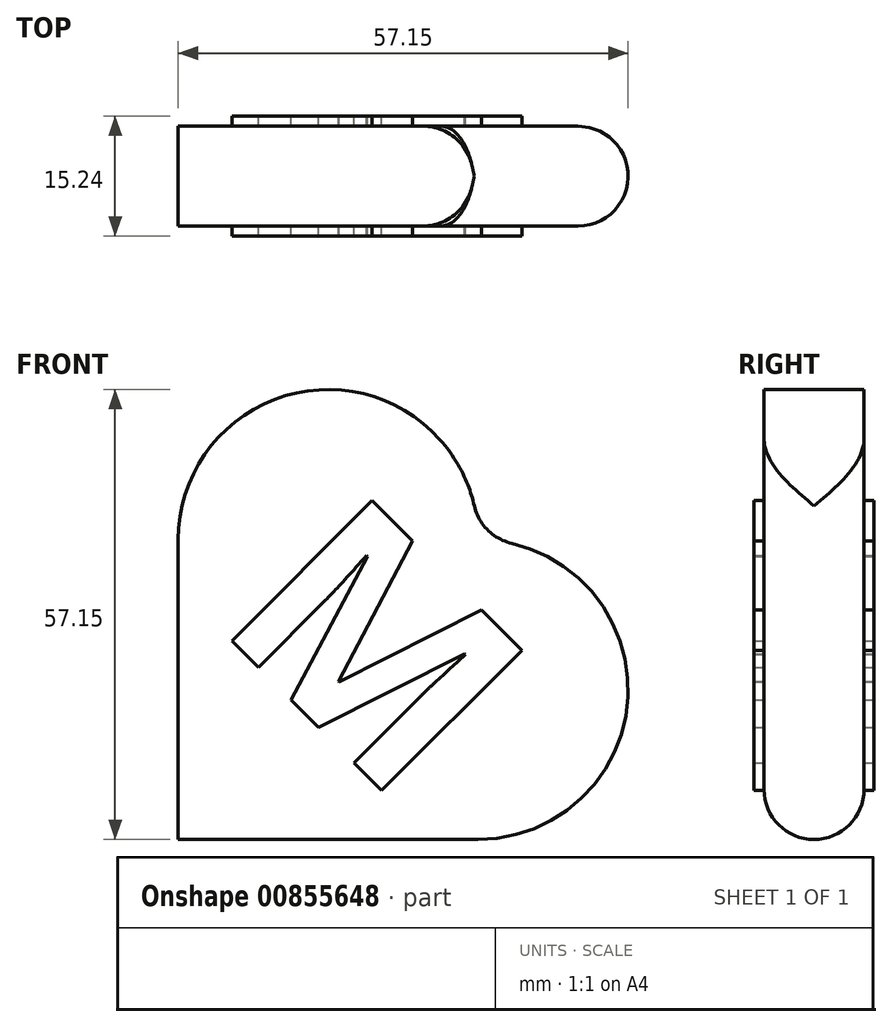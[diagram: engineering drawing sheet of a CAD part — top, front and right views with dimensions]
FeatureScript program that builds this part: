
annotation { "Feature Type Name" : "Feature", "Feature Type Description" : "" }
export const myFeature = defineFeature(function(context is Context, id is Id, definition is map)
    precondition{}
    {
        {
            var Q0;
            Q0=qCreatedBy(makeId("Front.planeOp"),FACE);
            var sketch = newSketch(context, id + "F0", { "sketchPlane" : qUnion([Q0])});
            skLineSegment(sketch, "E0.bottom", {"start": v(19.05, -19.05) * mm, "end": v(-19.05, -19.05) * mm});
            skLineSegment(sketch, "E0.top", {"start": v(19.05, 19.05) * mm, "end": v(-19.05, 19.05) * mm});
            skLineSegment(sketch, "E0.left", {"start": v(19.05, -19.05) * mm, "end": v(19.05, 19.05) * mm});
            skLineSegment(sketch, "E0.right", {"start": v(-19.05, -19.05) * mm, "end": v(-19.05, 19.05) * mm});
            skPoint(sketch, "E0.middle", {"position": v(0, 0) * mm});
            skCircle(sketch, "E1", {"center": v(0, 19.05) * mm, "radius": 19.05 * mm});
            skCircle(sketch, "E2", {"center": v(19.05, 0) * mm, "radius": 19.05 * mm});
            skSolve(sketch);
        }
        {
            var Q0;
            Q0 = qSketchRegion(id + "F0", true);
            extrude(context, id + "F1", {"entities" : qUnion([Q0]), "endBound" : BoundingType.SYMMETRIC, "depth" : 12.7 * mm, "offsetDistance" : 25.4 * mm});
        }
        {
            var Q0;
            Q0=makeQuery(id+"F1.opExtrude","SWEPT_FACE",FACE,{"disambiguationData":[OSD([sQuery(id+"F0.wireOp",EDGE,"E2")])]});
            fillet(context, id + "F2", {"entities" : qUnion([Q0]), "radius" : 6.35 * mm, "tangentPropagation" : true, "allowEdgeOverflow" : false});
        }
        {
            var Q0;
            Q0=qCreatedBy(makeId("Front.planeOp"),FACE);
            var sketch = newSketch(context, id + "F3", { "sketchPlane" : qUnion([Q0])});
            skText(sketch, "E3", { "text": "M", "fontName": "OpenSans-Bold.ttf"});
            const initialGuessF3  = {"E3": [-0.01447, 0.00843, 0.7071, -0.7071, 0.0254]};
            skSetInitialGuess(sketch, initialGuessF3);
            skSolve(sketch);
        }
        {
            var Q0;
            Q0 = qSketchRegion(id + "F3", true);
            extrude(context, id + "F4", {"entities" : qUnion([Q0]), "operationType" : NewBodyOperationType.ADD, "endBound" : BoundingType.SYMMETRIC, "depth" : 15.24 * mm, "offsetDistance" : 25.4 * mm});
        }
    });
